# Revit family: ALL1_63_UN_Downlighter_ETK
name_source: partatom
category: Lighting Fixtures
revit_build: Autodesk Revit 2017 (Build: 20190508_0315(x64)
units: mm (PartAtom-declared; Revit-internal decimal feet)

## family parameters
Always vertical = Yes
Cut with Voids When Loaded = No
Light Source = No
OmniClass Number = 23.80.70.11.14.11
OmniClass Title = Downlights
Part Type = Normal
Room Calculation Point = Yes
Round Connector Dimension = Use Diameter
Shared = No
Work Plane-Based = No

## types (16) — shared parameters
Assembly Code = 63.0
Bundle = 65°
IfcExportAs = IfcLightFixtureType
IfcExportType = USERDEFINED
Lamp = LED
Manufacturer = ETK B.V.
Model = ALL.1
URL = https://www.etk.nl
Voltage = 230 V

## per-type parameters (varying)
| type | Apparent Load | Light Source | Wattage Comments |
| ALL.1100.15 - 15W / 1500lm / 3000K | 15 VA | ALL.1 - Lightsource : ALL.1100.15 - 15W / 1500lm / 3000K | 15W |
| ALL.1103.15 - 15W / 1500lm / 3000K | 15 VA | ALL.1 - Lightsource : ALL.1103.15 - 15W / 1500lm / 3000K | 15W |
| ALL.1110.15 - 15W / 1500lm / 3000K | 15 VA | ALL.1 - Lightsource : ALL.1110.15 - 15W / 1500lm / 3000K | 15W |
| ALL.1113.15 - 15W / 1500lm / 3000K | 15 VA | ALL.1 - Lightsource : ALL.1113.15 - 15W / 1500lm / 3000K | 15W |
| ALL.1200.15 - 15W / 1600lm / 4000K | 15 VA | ALL.1 - Lightsource : ALL.1200.15 - 15W / 1600lm / 4000K | 15W |
| ALL.1203.15 - 15W / 1600lm / 4000K | 15 VA | ALL.1 - Lightsource : ALL.1203.15 - 15W / 1600lm / 4000K | 15W |
| ALL.1210.15 - 15W / 1600lm / 4000K | 15 VA | ALL.1 - Lightsource : ALL.1210.15 - 15W / 1600lm / 4000K | 15W |
| ALL.1213.15 - 15W / 1600lm / 4000K | 15 VA | ALL.1 - Lightsource : ALL.1213.15 - 15W / 1600lm / 4000K | 15W |
| ALL.1300.15 - 19W / 1950lm / 3000K | 19 VA | ALL.1 - Lightsource : ALL.1300.15 - 19W / 1950lm / 3000K | 19W |
| ALL.1303.15 - 19W / 1950lm / 3000K | 19 VA | ALL.1 - Lightsource : ALL.1303.15 - 19W / 1950lm / 3000K | 19W |
| ALL.1310.15 - 19W / 1950lm / 3000K | 19 VA | ALL.1 - Lightsource : ALL.1310.15 - 19W / 1950lm / 3000K | 19W |
| ALL.1313.15 - 19W / 1950lm / 3000K | 19 VA | ALL.1 - Lightsource : ALL.1313.15 - 19W / 1950lm / 3000K | 19W |
| ALL.1400.15 - 19W / 2050lm / 4000K | 19 VA | ALL.1 - Lightsource : ALL.1400.15 - 19W / 2050lm / 4000K | 19W |
| ALL.1403.15 - 19W / 2050lm / 4000K | 19 VA | ALL.1 - Lightsource : ALL.1403.15 - 19W / 2050lm / 4000K | 19W |
| ALL.1410.15 - 19W / 2050lm / 4000K | 19 VA | ALL.1 - Lightsource : ALL.1410.15 - 19W / 2050lm / 4000K | 19W |
| ALL.1413.15 - 19W / 2050lm / 4000K | 19 VA | ALL.1 - Lightsource : ALL.1413.15 - 19W / 2050lm / 4000K | 19W |

## geometry (parser evidence)
native form markers: Sweep x10
no freeform markers — native parametric forms only
